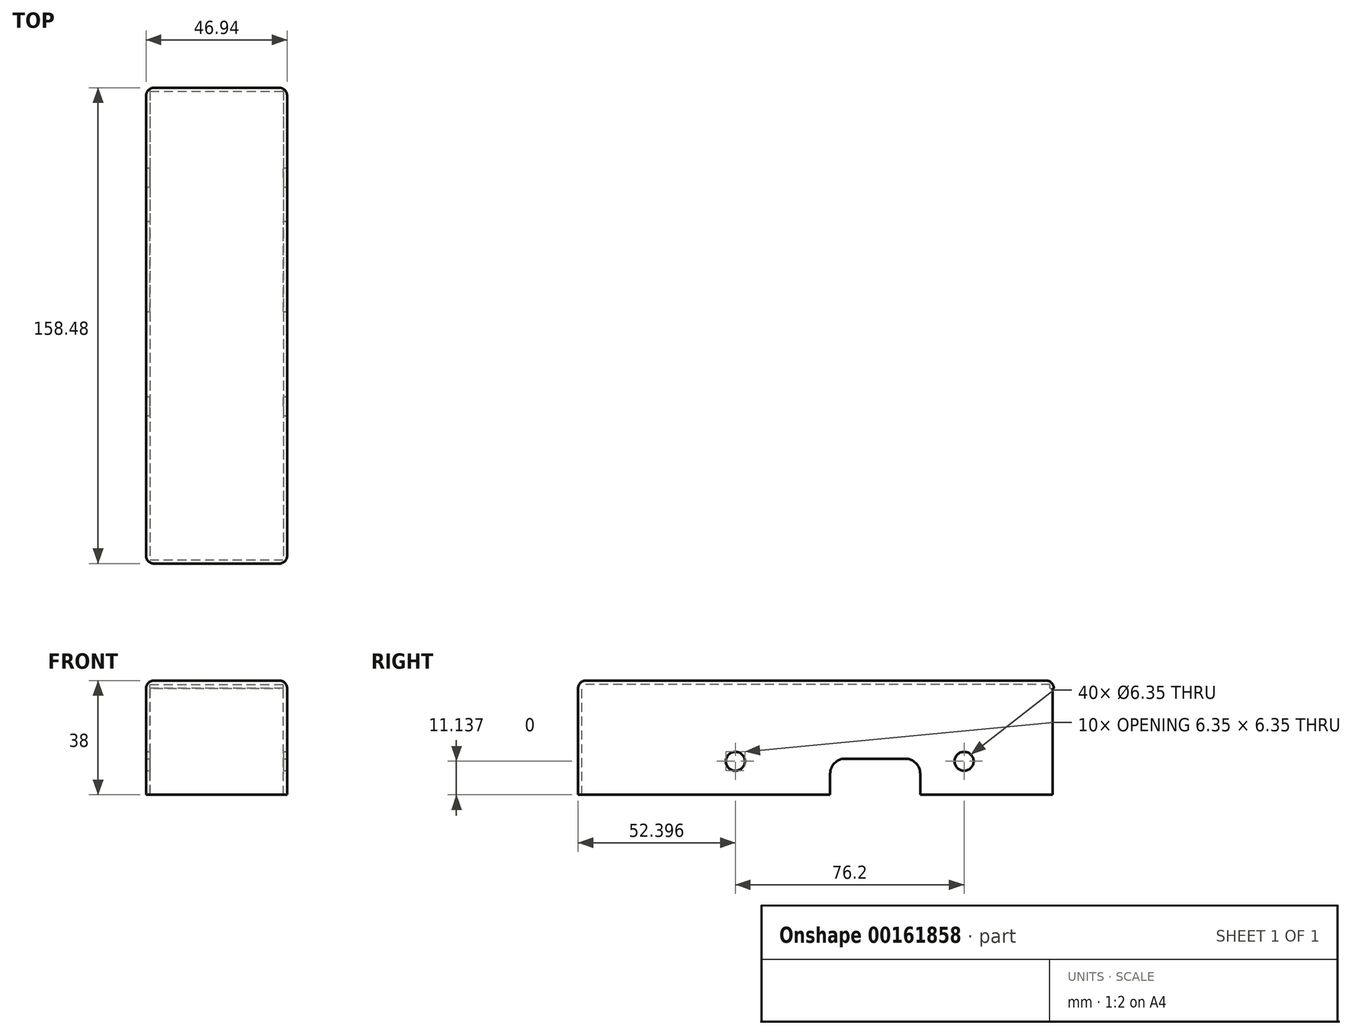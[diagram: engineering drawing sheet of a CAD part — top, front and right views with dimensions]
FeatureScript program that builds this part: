
annotation { "Feature Type Name" : "Feature", "Feature Type Description" : "" }
export const myFeature = defineFeature(function(context is Context, id is Id, definition is map)
    precondition{}
    {
        {
            var Q0;
            Q0=qCreatedBy(makeId("Top.planeOp"),FACE);
            var sketch = newSketch(context, id + "F0", { "sketchPlane" : qUnion([Q0])});
            skLineSegment(sketch, "E0.bottom", {"start": v(-23.47, 79.24) * mm, "end": v(23.47, 79.24) * mm});
            skLineSegment(sketch, "E0.top", {"start": v(-23.47, -79.24) * mm, "end": v(23.47, -79.24) * mm});
            skLineSegment(sketch, "E0.left", {"start": v(-23.47, 79.24) * mm, "end": v(-23.47, -79.24) * mm});
            skLineSegment(sketch, "E0.right", {"start": v(23.47, 79.24) * mm, "end": v(23.47, -79.24) * mm});
            skPoint(sketch, "E0.middle", {"position": v(0, 0) * mm});
            skSolve(sketch);
        }
        {
            var Q0;
            Q0=qSketchRegion(id+"F0",true);
            extrude(context, id + "F1", {"entities" : qUnion([Q0]), "oppositeDirection" : true, "depth" : 38 * mm});
        }
        {
            var Q0;
            Q0=makeQuery(id+"F1.opExtrude","CAP_FACE",FACE,{"disambiguationData":[OSD([sQuery(id+"F0.wireOp",EDGE,"E0.bottom"),sQuery(id+"F0.wireOp",EDGE,"E0.top"),sQuery(id+"F0.wireOp",EDGE,"E0.left"),sQuery(id+"F0.wireOp",EDGE,"E0.right")])],"isStart":false});
            shell(context, id + "F2", {"entities" : qUnion([Q0]), "thickness" : 1.22 * mm});
        }
        {
            var Q0;
            Q0=makeQuery(id+"F1.opExtrude","CAP_EDGE",EDGE,{"disambiguationData":[OSD([sQuery(id+"F0.wireOp",EDGE,"E0.right")])],"isStart":true});
            var Q1;
            Q1=makeQuery(id+"F1.opExtrude","CAP_EDGE",EDGE,{"disambiguationData":[OSD([sQuery(id+"F0.wireOp",EDGE,"E0.left")])],"isStart":true});
            var Q2;
            Q2=makeQuery(id+"F1.opExtrude","CAP_EDGE",EDGE,{"disambiguationData":[OSD([sQuery(id+"F0.wireOp",EDGE,"E0.top")])],"isStart":true});
            var Q3;
            Q3=makeQuery(id+"F1.opExtrude","SWEPT_EDGE",EDGE,{"disambiguationData":[OSD([sQuery(id+"F0.wireOp",EDGE,"E0.top"),sQuery(id+"F0.wireOp",EDGE,"E0.right")])]});
            var Q4;
            Q4=makeQuery(id+"F1.opExtrude","SWEPT_EDGE",EDGE,{"disambiguationData":[OSD([sQuery(id+"F0.wireOp",EDGE,"E0.top"),sQuery(id+"F0.wireOp",EDGE,"E0.left")])]});
            var Q5;
            Q5=makeQuery(id+"F1.opExtrude","SWEPT_EDGE",EDGE,{"disambiguationData":[OSD([sQuery(id+"F0.wireOp",EDGE,"E0.bottom"),sQuery(id+"F0.wireOp",EDGE,"E0.left")])]});
            var Q6;
            Q6=makeQuery(id+"F1.opExtrude","SWEPT_EDGE",EDGE,{"disambiguationData":[OSD([sQuery(id+"F0.wireOp",EDGE,"E0.bottom"),sQuery(id+"F0.wireOp",EDGE,"E0.right")])]});
            var Q7;
            Q7=makeQuery(id+"F1.opExtrude","CAP_EDGE",EDGE,{"disambiguationData":[OSD([sQuery(id+"F0.wireOp",EDGE,"E0.bottom")])],"isStart":true});
            fillet(context, id + "F3", {"entities" : qUnion([Q0, Q1, Q2, Q3, Q4, Q5, Q6, Q7]), "radius" : 2.54 * mm, "tangentPropagation" : true, "allowEdgeOverflow" : false});
        }
        {
            var Q0;
            Q0=makeQuery(id+"F1.opExtrude","SWEPT_FACE",FACE,{"disambiguationData":[OSD([sQuery(id+"F0.wireOp",EDGE,"E0.right")])]});
            var sketch = newSketch(context, id + "F4", { "sketchPlane" : qUnion([Q0])});
            skLineSegment(sketch, "E1.0", {"start": v(79.24, -2.54) * mm, "end": v(79.24, -38) * mm});
            skLineSegment(sketch, "E1.1", {"start": v(34.74, -38) * mm, "end": v(4.74, -38) * mm});
            skLineSegment(sketch, "E2.0", {"start": v(34.74, -31) * mm, "end": v(34.74, -38) * mm});
            skLineSegment(sketch, "E3.0", {"start": v(29.74, -26) * mm, "end": v(9.74, -26) * mm});
            skLineSegment(sketch, "E4.0", {"start": v(4.74, -31) * mm, "end": v(4.74, -38) * mm});
            skPoint(sketch, "E5.orphan", {"position": v(-76.7, -38) * mm});
            skPoint(sketch, "E6.orphan", {"position": v(76.7, -38) * mm});
            skArc(sketch, "E7", {"start": v(9.74, -26) * mm, "mid": v(6.2, -27.47) * mm, "end": v(4.74, -31) * mm});
            skArc(sketch, "E8", {"start": v(34.74, -31) * mm, "mid": v(33.28, -27.47) * mm, "end": v(29.74, -26) * mm});
            skSolve(sketch);
        }
        {
            var Q0;
            Q0=qSketchRegion(id+"F4",true);
            extrude(context, id + "F5", {"entities" : qUnion([Q0]), "operationType" : NewBodyOperationType.REMOVE, "endBound" : BoundingType.THROUGH_ALL, "oppositeDirection" : true, "depth" : 25.4 * mm});
        }
        {
            var Q0;
            Q0=makeQuery(id+"F1.opExtrude","SWEPT_FACE",FACE,{"disambiguationData":[OSD([sQuery(id+"F0.wireOp",EDGE,"E0.right")])]});
            var sketch = newSketch(context, id + "F6", { "sketchPlane" : qUnion([Q0])});
            skLineSegment(sketch, "E9.0", {"start": v(4.74, -38) * mm, "end": v(-76.7, -38) * mm});
            skLineSegment(sketch, "E9.1", {"start": v(-79.24, -38) * mm, "end": v(-79.24, -2.54) * mm});
            skCircle(sketch, "E10", {"center": v(-26.84, -26.86) * mm, "radius": 3.18 * mm});
            skCircle(sketch, "E11", {"center": v(49.36, -26.86) * mm, "radius": 3.18 * mm});
            skSolve(sketch);
        }
        {
            var Q0;
            Q0=qSketchRegion(id+"F6",true);
            extrude(context, id + "F7", {"entities" : qUnion([Q0]), "operationType" : NewBodyOperationType.REMOVE, "endBound" : BoundingType.THROUGH_ALL, "oppositeDirection" : true, "depth" : 25.4 * mm});
        }
        {
            var Q0;
            Q0=makeQuery(id+"F1.opExtrude","SWEPT_FACE",FACE,{"disambiguationData":[OSD([sQuery(id+"F0.wireOp",EDGE,"E0.bottom")])]});
            var sketch = newSketch(context, id + "F8", { "sketchPlane" : qUnion([Q0])});
            skLineSegment(sketch, "E12.0", {"start": v(-23.47, -38) * mm, "end": v(-23.47, -2.54) * mm});
            skLineSegment(sketch, "E12.1", {"start": v(23.47, -2.54) * mm, "end": v(23.47, -38) * mm});
            skLineSegment(sketch, "E13.0", {"start": v(22.25, -2.54) * mm, "end": v(22.25, -38) * mm});
            skLineSegment(sketch, "E14.0", {"start": v(-22.25, -38) * mm, "end": v(-22.25, -2.54) * mm});
            skLineSegment(sketch, "E15", {"start": v(-22.25, -2.54) * mm, "end": v(22.25, -2.54) * mm});
            skLineSegment(sketch, "E16", {"start": v(22.25, -38) * mm, "end": v(-22.25, -38) * mm});
            skSolve(sketch);
        }
        {
            var Q0;
            Q0=qSketchRegion(id+"F8",true);
            extrude(context, id + "F9", {"entities" : qUnion([Q0]), "operationType" : NewBodyOperationType.REMOVE, "endBound" : BoundingType.UP_TO_NEXT, "oppositeDirection" : true, "depth" : 25.4 * mm});
        }
    });
